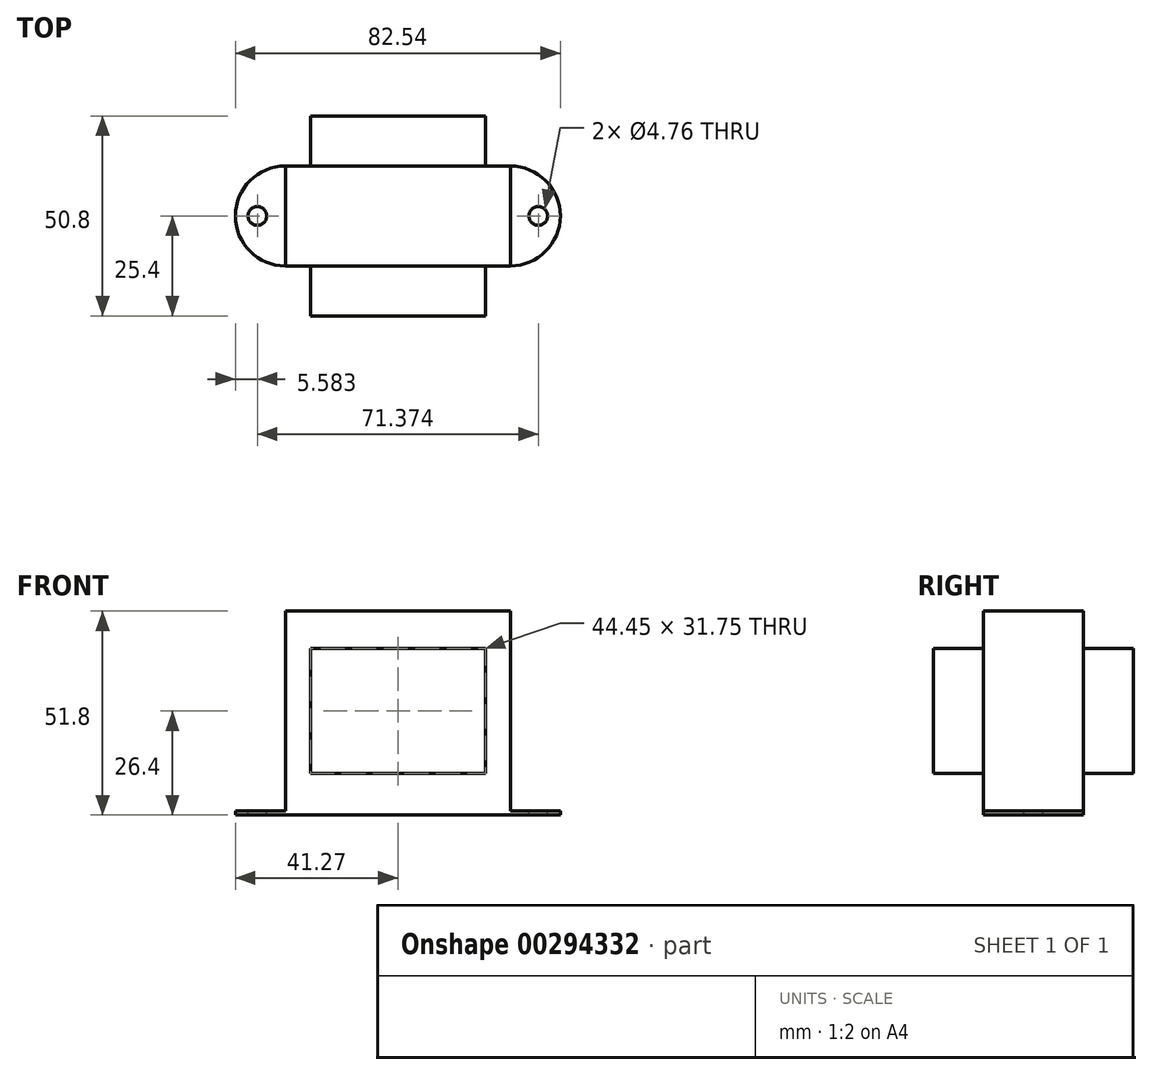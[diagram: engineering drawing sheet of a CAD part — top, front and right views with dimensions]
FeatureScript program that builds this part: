
annotation { "Feature Type Name" : "Feature", "Feature Type Description" : "" }
export const myFeature = defineFeature(function(context is Context, id is Id, definition is map)
    precondition{}
    {
        {
            var Q0;
            Q0=qCreatedBy(makeId("Top.planeOp"),FACE);
            var sketch = newSketch(context, id + "F0", { "sketchPlane" : qUnion([Q0])});
            skLineSegment(sketch, "E0.bottom", {"start": v(-28.58, -12.7) * mm, "end": v(28.58, -12.7) * mm});
            skLineSegment(sketch, "E0.top", {"start": v(-28.58, 12.7) * mm, "end": v(28.57, 12.7) * mm});
            skLineSegment(sketch, "E0.left", {"start": v(-28.57, -12.7) * mm, "end": v(-28.58, 12.7) * mm});
            skLineSegment(sketch, "E0.right", {"start": v(28.58, -12.7) * mm, "end": v(28.57, 12.7) * mm});
            skCircle(sketch, "E1", {"center": v(-28.58, 0) * mm, "radius": 12.7 * mm});
            skCircle(sketch, "E2", {"center": v(28.58, 0) * mm, "radius": 12.7 * mm});
            skLineSegment(sketch, "E3", {"start": v(0, 12.7) * mm, "end": v(0, -12.7) * mm, "construction": true});
            skSolve(sketch);
        }
        {
            var Q0;
            {var subQ0=sQuery(id+"F0.wireOp",EDGE,"E0.left");Q0=makeQuery(id+"F0.imprint","IMPRINT",FACE,{"disambiguationData":[TD([[makeQuery(id+"F0.imprint","IMPRINT",EDGE,{"derivedFrom":subQ0}),1.0]])]});}
            var Q1;
            {var subQ0=sQuery(id+"F0.wireOp",EDGE,"E0.left");Q1=makeQuery(id+"F0.imprint","IMPRINT",FACE,{"disambiguationData":[TD([[makeQuery(id+"F0.imprint","IMPRINT",EDGE,{"derivedFrom":subQ0}),-1.0]])]});}
            var Q2;
            {var subQ0=sQuery(id+"F0.wireOp",EDGE,"E0.bottom");Q2=makeQuery(id+"F0.imprint","IMPRINT",FACE,{"disambiguationData":[TD([[makeQuery(id+"F0.imprint","IMPRINT",EDGE,{"derivedFrom":subQ0}),1.0]])]});}
            var Q3;
            {var subQ0=sQuery(id+"F0.wireOp",EDGE,"E0.right");Q3=makeQuery(id+"F0.imprint","IMPRINT",FACE,{"disambiguationData":[TD([[makeQuery(id+"F0.imprint","IMPRINT",EDGE,{"derivedFrom":subQ0}),1.0]])]});}
            var Q4;
            {var subQ0=sQuery(id+"F0.wireOp",EDGE,"E0.right");Q4=makeQuery(id+"F0.imprint","IMPRINT",FACE,{"disambiguationData":[TD([[makeQuery(id+"F0.imprint","IMPRINT",EDGE,{"derivedFrom":subQ0}),-1.0]])]});}
            extrude(context, id + "F1", {"entities" : qUnion([Q0, Q1, Q2, Q3, Q4]), "depth" : 1 * mm});
        }
        {
            var Q0;
            Q0=makeQuery(id+"F1.opExtrude","CAP_FACE",FACE,{"disambiguationData":[OSD([sQuery(id+"F0.wireOp",EDGE,"E0.bottom"),sQuery(id+"F0.wireOp",EDGE,"E0.top"),sQuery(id+"F0.wireOp",EDGE,"E1"),sQuery(id+"F0.wireOp",EDGE,"E2")])],"isStart":false});
            var sketch = newSketch(context, id + "F2", { "sketchPlane" : qUnion([Q0])});
            skPoint(sketch, "E4", {"position": v(-35.69, 0) * mm});
            skPoint(sketch, "E5", {"position": v(35.69, 0) * mm});
            skSolve(sketch);
        }
        {
            var Q0;
            Q0=sQuery(id+"F2.wireOp",VERTEX,"E4");
            var Q1;
            Q1=sQuery(id+"F2.wireOp",VERTEX,"E5");
            var Q2;
            Q2=makeQuery(id+"F1.opExtrude","SWEPT_BODY",BODY,{"disambiguationData":[OSD([sQuery(id+"F0.wireOp",EDGE,"E0.bottom"),sQuery(id+"F0.wireOp",EDGE,"E0.top"),sQuery(id+"F0.wireOp",EDGE,"E1"),sQuery(id+"F0.wireOp",EDGE,"E2")])]});
            hole(context, id + "F3", {"style" : HoleStyle.SIMPLE, "endStyle" : HoleEndStyle.THROUGH, "holeDiameter" : 4.76 * mm, "tappedDepth" : 12.7 * mm, "tapClearance" : 3, "locations" : qUnion([Q0, Q1]), "scope" : qUnion([Q2])});
        }
        {
            var Q0;
            Q0=makeQuery(id+"F1.opExtrude","CAP_FACE",FACE,{"disambiguationData":[OSD([sQuery(id+"F0.wireOp",EDGE,"E0.bottom"),sQuery(id+"F0.wireOp",EDGE,"E0.top"),sQuery(id+"F0.wireOp",EDGE,"E1"),sQuery(id+"F0.wireOp",EDGE,"E2")])],"isStart":false});
            var sketch = newSketch(context, id + "F4", { "sketchPlane" : qUnion([Q0])});
            skLineSegment(sketch, "E6.bottom", {"start": v(-28.58, 12.7) * mm, "end": v(28.58, 12.7) * mm});
            skLineSegment(sketch, "E6.top", {"start": v(-28.58, -12.7) * mm, "end": v(28.58, -12.7) * mm});
            skLineSegment(sketch, "E6.left", {"start": v(-28.58, 12.7) * mm, "end": v(-28.58, -12.7) * mm});
            skLineSegment(sketch, "E6.right", {"start": v(28.58, 12.7) * mm, "end": v(28.58, -12.7) * mm});
            skSolve(sketch);
        }
        {
            var Q0;
            Q0=makeQuery(id+"F4.imprint","IMPRINT",FACE,{"disambiguationData":[TD([[makeQuery(id+"F4.imprint","IMPRINT",EDGE,{"derivedFrom":sQuery(id+"F4.wireOp",EDGE,"E6.bottom")}),-1.0]])]});
            extrude(context, id + "F5", {"entities" : qUnion([Q0]), "operationType" : NewBodyOperationType.ADD, "depth" : 50.8 * mm});
        }
        {
            var Q0;
            Q0=qCreatedBy(makeId("Front.planeOp"),FACE);
            var sketch = newSketch(context, id + "F6", { "sketchPlane" : qUnion([Q0])});
            skLineSegment(sketch, "E7.0.0", {"start": v(-28.58, 0) * mm, "end": v(28.58, 0) * mm});
            skLineSegment(sketch, "E7.0.1", {"start": v(28.58, 0) * mm, "end": v(28.58, 1) * mm});
            skLineSegment(sketch, "E7.0.2", {"start": v(28.58, 1) * mm, "end": v(28.58, 51.8) * mm});
            skLineSegment(sketch, "E7.0.3", {"start": v(28.58, 51.8) * mm, "end": v(-28.58, 51.8) * mm, "construction": true});
            skLineSegment(sketch, "E7.0.4", {"start": v(-28.58, 51.8) * mm, "end": v(-28.58, 1) * mm});
            skLineSegment(sketch, "E7.0.5", {"start": v(-28.58, 1) * mm, "end": v(-28.58, 0) * mm});
            skLineSegment(sketch, "E8.bottom", {"start": v(-22.23, 42.28) * mm, "end": v(22.23, 42.28) * mm});
            skLineSegment(sketch, "E8.top", {"start": v(-22.22, 10.52) * mm, "end": v(22.22, 10.53) * mm});
            skLineSegment(sketch, "E8.left", {"start": v(-22.22, 42.28) * mm, "end": v(-22.22, 10.53) * mm});
            skLineSegment(sketch, "E8.right", {"start": v(22.23, 42.28) * mm, "end": v(22.23, 10.53) * mm});
            skLineSegment(sketch, "E9", {"start": v(0, 51.8) * mm, "end": v(0, 0) * mm, "construction": true});
            skSolve(sketch);
        }
        {
            var Q0;
            Q0 = qSketchRegion(id + "F6", true);
            extrude(context, id + "F7", {"entities" : qUnion([Q0]), "operationType" : NewBodyOperationType.ADD, "endBound" : BoundingType.SYMMETRIC, "depth" : 50.8 * mm});
        }
    });
